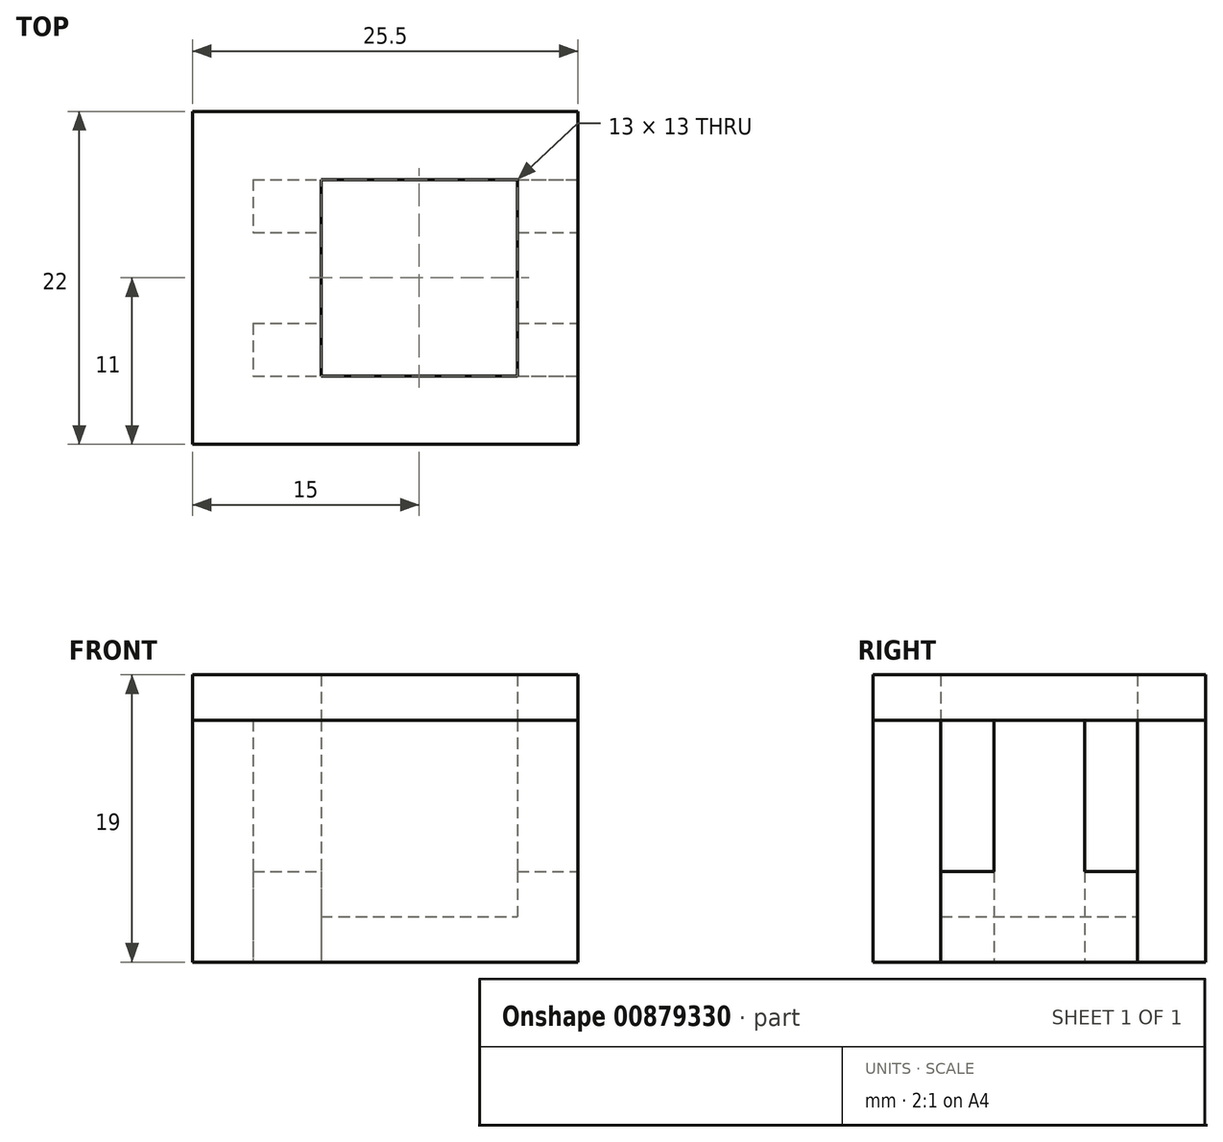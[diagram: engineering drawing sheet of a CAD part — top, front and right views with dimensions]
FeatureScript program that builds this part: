
annotation { "Feature Type Name" : "Feature", "Feature Type Description" : "" }
export const myFeature = defineFeature(function(context is Context, id is Id, definition is map)
    precondition{}
    {
        {
            var Q0;
            Q0=qCreatedBy(makeId("Top.planeOp"),FACE);
            var sketch = newSketch(context, id + "F0", { "sketchPlane" : qUnion([Q0])});
            skLineSegment(sketch, "E0.bottom", {"start": v(0, 0) * mm, "end": v(-25.5, 0) * mm});
            skLineSegment(sketch, "E0.top", {"start": v(0, 11) * mm, "end": v(-16.5, 11) * mm});
            skLineSegment(sketch, "E0.left", {"start": v(0, 0) * mm, "end": v(0, 4.5) * mm});
            skLineSegment(sketch, "E0.right", {"start": v(-25.5, 0) * mm, "end": v(-25.5, 11) * mm});
            skLineSegment(sketch, "E1", {"start": v(-21.5, 4.5) * mm, "end": v(0, 4.5) * mm});
            skLineSegment(sketch, "E2", {"start": v(-21.5, 11) * mm, "end": v(-21.5, 11) * mm});
            skLineSegment(sketch, "E3.bottom", {"start": v(-16.5, 5) * mm, "end": v(-4, 5) * mm, "construction": true});
            skLineSegment(sketch, "E3.top", {"start": v(-16.5, 17) * mm, "end": v(-4, 17) * mm, "construction": true});
            skLineSegment(sketch, "E3.left", {"start": v(-16.5, 5) * mm, "end": v(-16.5, 11) * mm, "construction": true});
            skLineSegment(sketch, "E4.bottom", {"start": v(-21.5, 7.5) * mm, "end": v(-17, 7.5) * mm, "construction": true});
            skLineSegment(sketch, "E4.left", {"start": v(-21.5, 7.5) * mm, "end": v(-21.5, 5) * mm, "construction": true});
            skLineSegment(sketch, "E4.right", {"start": v(0.5, 7.5) * mm, "end": v(0.5, 5) * mm, "construction": true});
            skLineSegment(sketch, "E5", {"start": v(-21.5, 8) * mm, "end": v(-17, 8) * mm});
            skLineSegment(sketch, "E6", {"start": v(-17, 11) * mm, "end": v(-17, 8) * mm});
            skLineSegment(sketch, "E7", {"start": v(0, 4.5) * mm, "end": v(0, 4.5) * mm});
            skLineSegment(sketch, "E8", {"start": v(0, 4.5) * mm, "end": v(0, 11) * mm});
            skLineSegment(sketch, "E9", {"start": v(-17, 11) * mm, "end": v(-21.5, 11) * mm});
            skLineSegment(sketch, "E10", {"start": v(-21.5, 11) * mm, "end": v(-21.5, 8) * mm});
            skLineSegment(sketch, "E11", {"start": v(-21.5, 11) * mm, "end": v(-25.5, 11) * mm});
            skPoint(sketch, "E12", {"position": v(-16.5, 11) * mm});
            skLineSegment(sketch, "E13", {"start": v(-16.5, 11) * mm, "end": v(-16.5, 17) * mm, "construction": true});
            skLineSegment(sketch, "E14", {"start": v(-16.5, 11) * mm, "end": v(-17, 11) * mm});
            skLineSegment(sketch, "E15.MirrorCS", {"start": v(-21.5, 14.5) * mm, "end": v(-17, 14.5) * mm, "construction": true});
            skLineSegment(sketch, "E16.MirrorCS", {"start": v(-21.5, 17.5) * mm, "end": v(0, 17.5) * mm});
            skLineSegment(sketch, "E17.MirrorCS", {"start": v(0, 17.5) * mm, "end": v(0, 11) * mm});
            skLineSegment(sketch, "E18.MirrorCS", {"start": v(-21.5, 14.5) * mm, "end": v(-21.5, 17) * mm, "construction": true});
            skLineSegment(sketch, "E19.MirrorCS", {"start": v(0.5, 14.5) * mm, "end": v(0.5, 17) * mm, "construction": true});
            skLineSegment(sketch, "E20.MirrorCS", {"start": v(0, 22) * mm, "end": v(0, 17.5) * mm});
            skLineSegment(sketch, "E21.MirrorCS", {"start": v(0, 22) * mm, "end": v(-25.5, 22) * mm});
            skLineSegment(sketch, "E22.MirrorCS", {"start": v(-21.5, 14) * mm, "end": v(-17, 14) * mm});
            skLineSegment(sketch, "E23.MirrorCS", {"start": v(-17, 11) * mm, "end": v(-17, 14) * mm});
            skLineSegment(sketch, "E24.MirrorCS", {"start": v(-25.5, 22) * mm, "end": v(-25.5, 11) * mm});
            skLineSegment(sketch, "E25", {"start": v(-21.5, 14.5) * mm, "end": v(-21.5, 14) * mm});
            skLineSegment(sketch, "E26", {"start": v(-21.5, 17.5) * mm, "end": v(-21.5, 14) * mm});
            skLineSegment(sketch, "E27", {"start": v(-17, 8) * mm, "end": v(-17, 7.5) * mm});
            skLineSegment(sketch, "E28", {"start": v(-17, 14) * mm, "end": v(-17, 14.5) * mm});
            skLineSegment(sketch, "E29", {"start": v(-21.5, 7.5) * mm, "end": v(-21.5, 4.5) * mm});
            skLineSegment(sketch, "E30", {"start": v(-21.5, 8) * mm, "end": v(-21.5, 7.5) * mm});
            skLineSegment(sketch, "E31", {"start": v(-17, 7.5) * mm, "end": v(-4, 7.5) * mm, "construction": true});
            skLineSegment(sketch, "E32", {"start": v(-17, 14.5) * mm, "end": v(-4, 14.5) * mm, "construction": true});
            skLineSegment(sketch, "E33", {"start": v(0, 14.5) * mm, "end": v(0.5, 14.5) * mm});
            skLineSegment(sketch, "E34", {"start": v(0, 7.5) * mm, "end": v(0.5, 7.5) * mm});
            skLineSegment(sketch, "E35", {"start": v(-17, 7.5) * mm, "end": v(-17, 4.5) * mm});
            skLineSegment(sketch, "E36", {"start": v(-4, 7.5) * mm, "end": v(0, 7.5) * mm, "construction": true});
            skLineSegment(sketch, "E37", {"start": v(-4, 7.5) * mm, "end": v(-4, 17) * mm});
            skLineSegment(sketch, "E38", {"start": v(-4, 7.5) * mm, "end": v(-4, 5) * mm});
            skLineSegment(sketch, "E39", {"start": v(-4, 5) * mm, "end": v(0, 5) * mm, "construction": true});
            skLineSegment(sketch, "E40", {"start": v(0, 5) * mm, "end": v(0.5, 5) * mm});
            skLineSegment(sketch, "E41", {"start": v(-16.5, 5) * mm, "end": v(-17, 5) * mm});
            skLineSegment(sketch, "E42", {"start": v(-17, 5) * mm, "end": v(-21.5, 5) * mm, "construction": true});
            skLineSegment(sketch, "E43", {"start": v(-21.5, 17) * mm, "end": v(-16.5, 17) * mm, "construction": true});
            skLineSegment(sketch, "E44", {"start": v(-4, 17) * mm, "end": v(0, 17) * mm, "construction": true});
            skLineSegment(sketch, "E45", {"start": v(0, 17) * mm, "end": v(0.5, 17) * mm});
            skLineSegment(sketch, "E46", {"start": v(-17, 14.5) * mm, "end": v(-17, 17) * mm});
            skLineSegment(sketch, "E47", {"start": v(-17, 17) * mm, "end": v(-17, 17.5) * mm});
            skLineSegment(sketch, "E48", {"start": v(-4, 14.5) * mm, "end": v(0, 14.5) * mm, "construction": true});
            skLineSegment(sketch, "E49", {"start": v(-4, 5) * mm, "end": v(-4, 4.5) * mm});
            skLineSegment(sketch, "E50", {"start": v(-4, 17) * mm, "end": v(-4, 17.5) * mm});
            skLineSegment(sketch, "E51", {"start": v(-17, 14) * mm, "end": v(-4, 14) * mm, "construction": true});
            skLineSegment(sketch, "E52", {"start": v(-4, 14) * mm, "end": v(0, 14) * mm});
            skLineSegment(sketch, "E53", {"start": v(-17, 8) * mm, "end": v(-4, 8) * mm, "construction": true});
            skLineSegment(sketch, "E54", {"start": v(-4, 8) * mm, "end": v(0, 8) * mm});
            skSolve(sketch);
        }
        {
            var Q0;
            Q0=makeQuery(id+"F0.imprint","IMPRINT",FACE,{"disambiguationData":[TD([[makeQuery(id+"F0.imprint","IMPRINT",EDGE,{"derivedFrom":sQuery(id+"F0.wireOp",EDGE,"E9")}),-1.0]])]});
            var Q1;
            Q1=makeQuery(id+"F0.imprint","IMPRINT",FACE,{"disambiguationData":[TD([[makeQuery(id+"F0.imprint","IMPRINT",EDGE,{"derivedFrom":sQuery(id+"F0.wireOp",EDGE,"E0.bottom")}),-1.0]])]});
            var Q2;
            Q2=makeQuery(id+"F0.imprint","IMPRINT",FACE,{"disambiguationData":[TD([[makeQuery(id+"F0.imprint","IMPRINT",EDGE,{"derivedFrom":sQuery(id+"F0.wireOp",EDGE,"E5")}),1.0]])]});
            extrude(context, id + "F1", {"entities" : qUnion([Q0, Q1, Q2]), "depth" : 16 * mm, "offsetDistance" : 25 * mm});
        }
        {
            var Q0;
            Q0=makeQuery(id+"F0.imprint","IMPRINT",FACE,{"disambiguationData":[TD([[makeQuery(id+"F0.imprint","IMPRINT",EDGE,{"derivedFrom":sQuery(id+"F0.wireOp",EDGE,"E5")}),-1.0]])]});
            var Q1;
            {var subQ1=sQuery(id+"F0.wireOp",EDGE,"E22.MirrorCS");Q1=makeQuery(id+"F0.imprint","IMPRINT",FACE,{"disambiguationData":[TD([[makeQuery(id+"F0.imprint","IMPRINT",EDGE,{"derivedFrom":subQ1}),1.0]])]});}
            var Q2;
            {var subQ6=sQuery(id+"F0.wireOp",EDGE,"E50");Q2=makeQuery(id+"F0.imprint","IMPRINT",FACE,{"disambiguationData":[TD([[makeQuery(id+"F0.imprint","IMPRINT",EDGE,{"derivedFrom":subQ6}),-1.0]])]});}
            var Q3;
            {var subQ7=sQuery(id+"F0.wireOp",EDGE,"E38");Q3=makeQuery(id+"F0.imprint","IMPRINT",FACE,{"disambiguationData":[TD([[makeQuery(id+"F0.imprint","IMPRINT",EDGE,{"derivedFrom":subQ7}),1.0]])]});}
            extrude(context, id + "F2", {"entities" : qUnion([Q0, Q1, Q2, Q3]), "depth" : 6 * mm, "offsetDistance" : 25 * mm});
        }
        {
            var Q0;
            {var subQ0=sQuery(id+"F0.wireOp",EDGE,"E14");Q0=makeQuery(id+"F0.imprint","IMPRINT",FACE,{"disambiguationData":[TD([[makeQuery(id+"F0.imprint","IMPRINT",EDGE,{"derivedFrom":subQ0}),-1.0]])]});}
            var Q1;
            Q1=makeQuery(id+"F0.imprint","IMPRINT",FACE,{"disambiguationData":[TD([[makeQuery(id+"F0.imprint","IMPRINT",EDGE,{"derivedFrom":sQuery(id+"F0.wireOp",EDGE,"E6")}),1.0]])]});
            extrude(context, id + "F3", {"entities" : qUnion([Q0, Q1]), "depth" : 3 * mm, "offsetDistance" : 25 * mm});
        }
        {
            var Q0;
            {var subQ5=sQuery(id+"F0.wireOp",EDGE,"E54");Q0=makeQuery(id+"F0.imprint","IMPRINT",FACE,{"disambiguationData":[TD([[makeQuery(id+"F0.imprint","IMPRINT",EDGE,{"derivedFrom":subQ5}),1.0]])]});}
            var Q1;
            {var subQ5=sQuery(id+"F0.wireOp",EDGE,"E52");Q1=makeQuery(id+"F0.imprint","IMPRINT",FACE,{"disambiguationData":[TD([[makeQuery(id+"F0.imprint","IMPRINT",EDGE,{"derivedFrom":subQ5}),-1.0]])]});}
            extrude(context, id + "F4", {"entities" : qUnion([Q0, Q1]), "operationType" : NewBodyOperationType.ADD, "depth" : 16 * mm, "offsetDistance" : 25 * mm});
        }
        {
            var Q0;
            Q0=makeQuery(id+"F1.opExtrude","CAP_FACE",FACE,{"disambiguationData":[OSD([sQuery(id+"F0.wireOp",EDGE,"E0.bottom"),sQuery(id+"F0.wireOp",EDGE,"E0.left"),sQuery(id+"F0.wireOp",EDGE,"E0.right"),sQuery(id+"F0.wireOp",EDGE,"E1"),sQuery(id+"F0.wireOp",EDGE,"E5"),sQuery(id+"F0.wireOp",EDGE,"E6"),sQuery(id+"F0.wireOp",EDGE,"E16.MirrorCS"),sQuery(id+"F0.wireOp",EDGE,"E20.MirrorCS"),sQuery(id+"F0.wireOp",EDGE,"E21.MirrorCS"),sQuery(id+"F0.wireOp",EDGE,"E22.MirrorCS"),sQuery(id+"F0.wireOp",EDGE,"E23.MirrorCS"),sQuery(id+"F0.wireOp",EDGE,"E24.MirrorCS"),sQuery(id+"F0.wireOp",EDGE,"E26"),sQuery(id+"F0.wireOp",EDGE,"E29"),sQuery(id+"F0.wireOp",EDGE,"E30")])],"isStart":false});
            var sketch = newSketch(context, id + "F5", { "sketchPlane" : qUnion([Q0])});
            skLineSegment(sketch, "E55", {"start": v(-4, 4.5) * mm, "end": v(-4, 17.5) * mm});
            skLineSegment(sketch, "E56", {"start": v(0, 4.5) * mm, "end": v(0, 17.5) * mm});
            skLineSegment(sketch, "E57", {"start": v(-17, 8) * mm, "end": v(-17, 4.5) * mm});
            skLineSegment(sketch, "E58", {"start": v(-17, 14) * mm, "end": v(-17, 17.5) * mm});
            skSolve(sketch);
        }
        {
            var Q0;
            {var subQ0=sQuery(id+"F5.wireOp",EDGE,"E57");Q0=makeQuery(id+"F5.imprint","IMPRINT",FACE,{"disambiguationData":[TD([[makeQuery(id+"F5.imprint","IMPRINT",EDGE,{"derivedFrom":subQ0}),-1.0]])]});}
            var Q1;
            {var subQ0=sQuery(id+"F5.wireOp",EDGE,"E58");Q1=makeQuery(id+"F5.imprint","IMPRINT",FACE,{"disambiguationData":[TD([[makeQuery(id+"F5.imprint","IMPRINT",EDGE,{"derivedFrom":subQ0}),1.0]])]});}
            var Q2;
            {var subQ0=sQuery(id+"F5.wireOp",EDGE,"E55");Q2=makeQuery(id+"F5.imprint","IMPRINT",FACE,{"disambiguationData":[TD([[makeQuery(id+"F5.imprint","IMPRINT",EDGE,{"derivedFrom":subQ0}),-1.0]])]});}
            var Q3;
            Q3=makeQuery(id+"F5.imprint","IMPRINT",FACE,{"disambiguationData":[TD([[makeQuery(id+"F5.imprint","IMPRINT",EDGE,{"derivedFrom":makeQuery(id+"F1.opExtrude","CAP_EDGE",EDGE,{"disambiguationData":[OSD([sQuery(id+"F0.wireOp",EDGE,"E0.bottom")])],"isStart":false})}),-1.0]])]});
            extrude(context, id + "F6", {"entities" : qUnion([Q0, Q1, Q2, Q3]), "depth" : 3 * mm, "offsetDistance" : 25 * mm});
        }
    });
